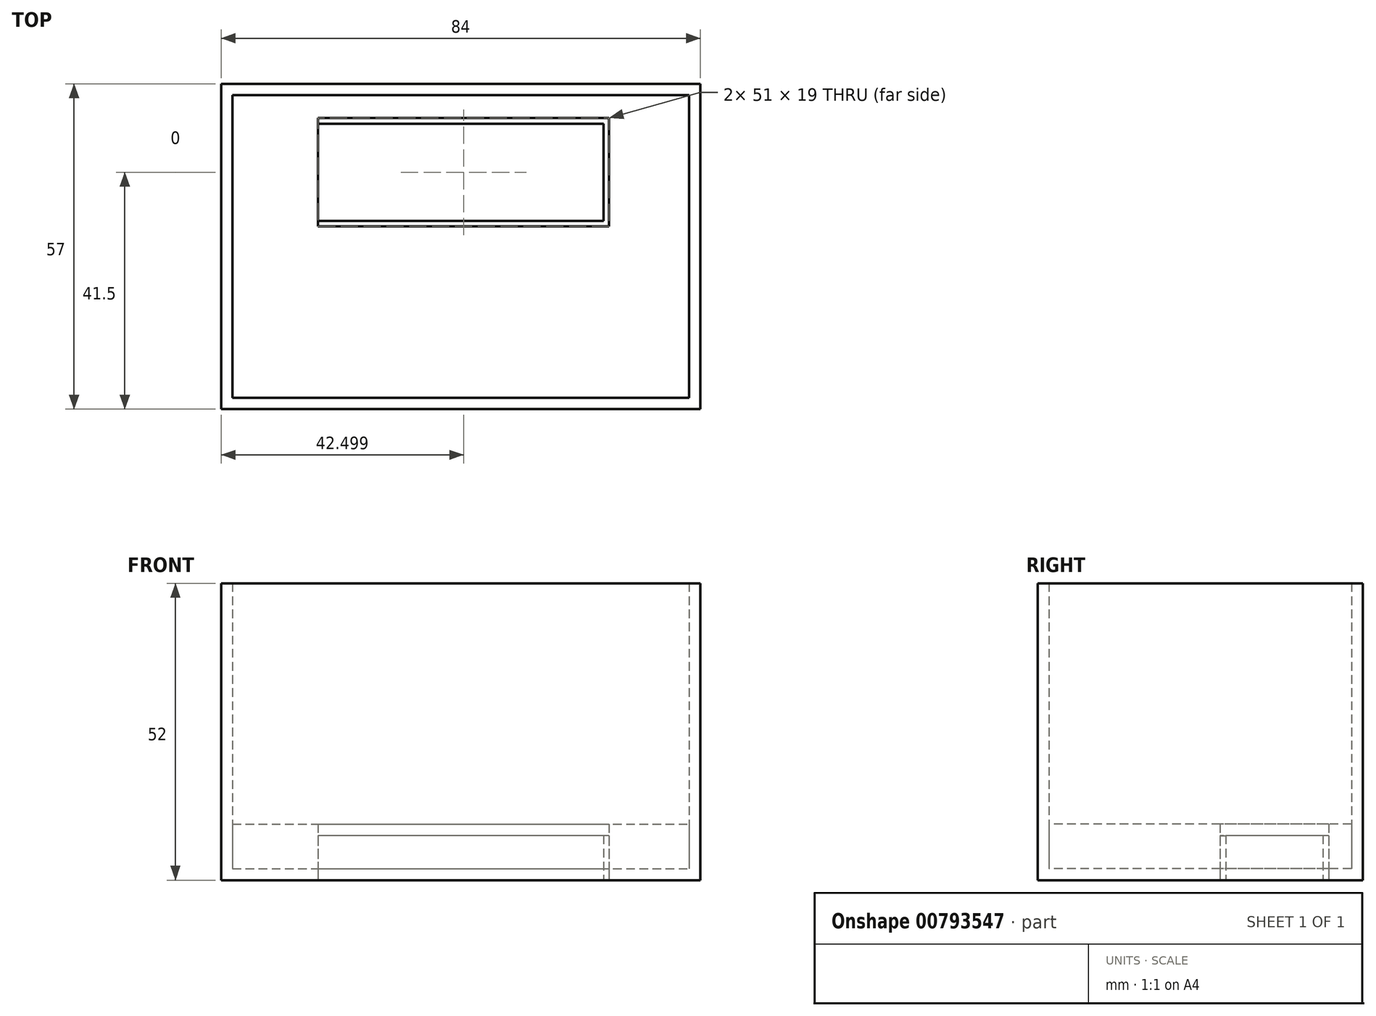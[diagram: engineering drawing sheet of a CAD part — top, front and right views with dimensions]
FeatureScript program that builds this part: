
annotation { "Feature Type Name" : "Feature", "Feature Type Description" : "" }
export const myFeature = defineFeature(function(context is Context, id is Id, definition is map)
    precondition{}
    {
        {
            var Q0;
            Q0=qCreatedBy(makeId("Top.planeOp"),FACE);
            var sketch = newSketch(context, id + "F0", { "sketchPlane" : qUnion([Q0])});
            skLineSegment(sketch, "E0", {"start": v(-45.1, 43.01) * mm, "end": v(4.9, 43.01) * mm});
            skLineSegment(sketch, "E1", {"start": v(4.9, 43.01) * mm, "end": v(4.9, 26.01) * mm});
            skLineSegment(sketch, "E2", {"start": v(4.9, 26.01) * mm, "end": v(-45.1, 26.01) * mm});
            skLineSegment(sketch, "E3", {"start": v(-45.1, 26.01) * mm, "end": v(-45.1, 43.01) * mm});
            skLineSegment(sketch, "E4", {"start": v(19.9, 48.01) * mm, "end": v(19.9, -4.99) * mm});
            skLineSegment(sketch, "E5", {"start": v(19.9, -4.99) * mm, "end": v(-60.1, -4.99) * mm});
            skLineSegment(sketch, "E6", {"start": v(-60.1, -4.99) * mm, "end": v(-60.1, 48.01) * mm});
            skLineSegment(sketch, "E7", {"start": v(-60.1, 48.01) * mm, "end": v(19.9, 48.01) * mm});
            skLineSegment(sketch, "E8", {"start": v(-62.1, 50.01) * mm, "end": v(21.9, 50.01) * mm});
            skLineSegment(sketch, "E9", {"start": v(21.9, 50.01) * mm, "end": v(21.9, -6.99) * mm});
            skLineSegment(sketch, "E10", {"start": v(21.9, -6.99) * mm, "end": v(-62.1, -6.99) * mm});
            skLineSegment(sketch, "E11", {"start": v(-62.1, 50.01) * mm, "end": v(-62.1, -6.99) * mm});
            skLineSegment(sketch, "E12", {"start": v(-45.1, 44.01) * mm, "end": v(5.9, 44.01) * mm});
            skLineSegment(sketch, "E13", {"start": v(-45.1, 44.01) * mm, "end": v(-45.1, 43.01) * mm});
            skLineSegment(sketch, "E14", {"start": v(5.9, 44.01) * mm, "end": v(5.9, 25.01) * mm});
            skLineSegment(sketch, "E15", {"start": v(5.9, 25.01) * mm, "end": v(-45.1, 25.01) * mm});
            skLineSegment(sketch, "E16", {"start": v(-45.1, 25.01) * mm, "end": v(-45.1, 26.01) * mm});
            skSolve(sketch);
        }
        {
            var Q0;
            Q0=makeQuery(id+"F0.imprint","IMPRINT",FACE,{"disambiguationData":[TD([[makeQuery(id+"F0.imprint","IMPRINT",EDGE,{"derivedFrom":sQuery(id+"F0.wireOp",EDGE,"E4")}),1.0]])]});
            extrude(context, id + "F1", {"entities" : qUnion([Q0]), "depth" : 52 * mm, "offsetDistance" : 25 * mm});
        }
        {
            var Q0;
            Q0=makeQuery(id+"F0.imprint","IMPRINT",FACE,{"disambiguationData":[TD([[makeQuery(id+"F0.imprint","IMPRINT",EDGE,{"derivedFrom":sQuery(id+"F0.wireOp",EDGE,"E3")}),1.0]])]});
            extrude(context, id + "F2", {"entities" : qUnion([Q0]), "operationType" : NewBodyOperationType.ADD, "depth" : 2 * mm, "offsetDistance" : 25 * mm});
        }
        {
            var Q0;
            Q0=makeQuery(id+"F0.imprint","IMPRINT",FACE,{"disambiguationData":[TD([[makeQuery(id+"F0.imprint","IMPRINT",EDGE,{"derivedFrom":sQuery(id+"F0.wireOp",EDGE,"E0")}),1.0]])]});
            var Q1;
            Q1=makeQuery(id+"F2.opExtrude","CAP_FACE",FACE,{"disambiguationData":[OSD([sQuery(id+"F0.wireOp",EDGE,"E3"),sQuery(id+"F0.wireOp",EDGE,"E4"),sQuery(id+"F0.wireOp",EDGE,"E5"),sQuery(id+"F0.wireOp",EDGE,"E6"),sQuery(id+"F0.wireOp",EDGE,"E7"),sQuery(id+"F0.wireOp",EDGE,"E12"),sQuery(id+"F0.wireOp",EDGE,"E13"),sQuery(id+"F0.wireOp",EDGE,"E14"),sQuery(id+"F0.wireOp",EDGE,"E15"),sQuery(id+"F0.wireOp",EDGE,"E16")])],"isStart":false});
            extrude(context, id + "F3", {"entities" : qUnion([Q0, Q1]), "depth" : 7.8 * mm, "offsetDistance" : 25 * mm});
        }
    });
